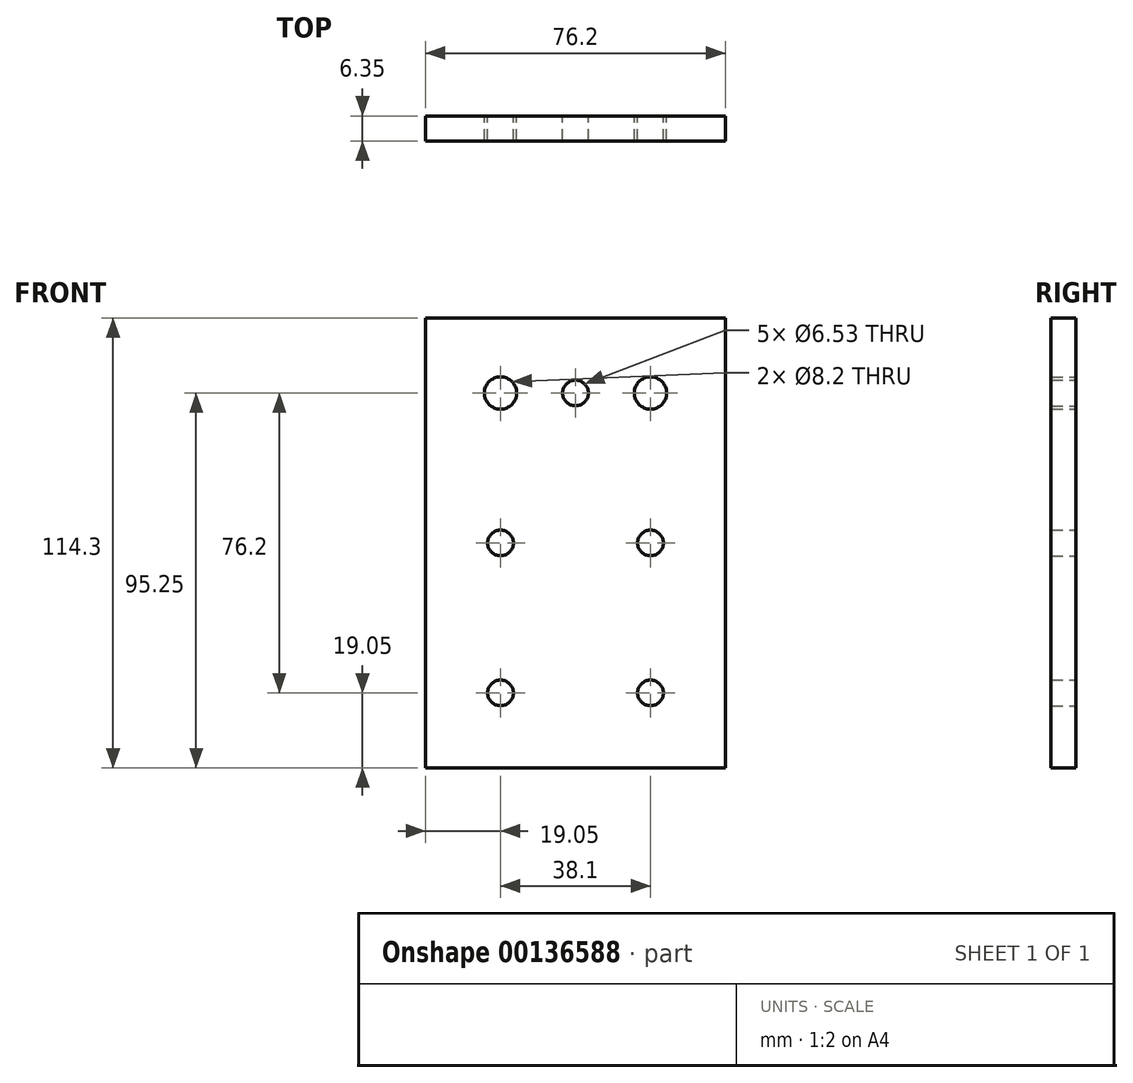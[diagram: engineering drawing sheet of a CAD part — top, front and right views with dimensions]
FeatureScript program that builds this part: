
annotation { "Feature Type Name" : "Feature", "Feature Type Description" : "" }
export const myFeature = defineFeature(function(context is Context, id is Id, definition is map)
    precondition{}
    {
        {
            var Q0;
            Q0=qCreatedBy(makeId("Front.planeOp"),FACE);
            var sketch = newSketch(context, id + "F0", { "sketchPlane" : qUnion([Q0])});
            skLineSegment(sketch, "E0.bottom", {"start": v(0, 0) * mm, "end": v(76.2, 0) * mm});
            skLineSegment(sketch, "E0.top", {"start": v(0, 114.3) * mm, "end": v(76.2, 114.3) * mm});
            skLineSegment(sketch, "E0.left", {"start": v(0, 0) * mm, "end": v(0, 114.3) * mm});
            skLineSegment(sketch, "E0.right", {"start": v(76.2, 0) * mm, "end": v(76.2, 114.3) * mm});
            skCircle(sketch, "E1", {"center": v(19.05, 95.25) * mm, "radius": 4.1 * mm});
            skLineSegment(sketch, "E2", {"start": v(38.1, 114.3) * mm, "end": v(38.1, 0) * mm, "construction": true});
            skCircle(sketch, "E3", {"center": v(19.05, 57.15) * mm, "radius": 3.26 * mm});
            skCircle(sketch, "E4", {"center": v(19.05, 19.05) * mm, "radius": 3.26 * mm});
            skCircle(sketch, "E5.MirrorC", {"center": v(57.15, 95.25) * mm, "radius": 4.1 * mm});
            skCircle(sketch, "E6.MirrorC", {"center": v(57.15, 57.15) * mm, "radius": 3.26 * mm});
            skCircle(sketch, "E7.MirrorC", {"center": v(57.15, 19.05) * mm, "radius": 3.26 * mm});
            skCircle(sketch, "E8", {"center": v(38.1, 95.25) * mm, "radius": 3.26 * mm});
            skSolve(sketch);
        }
        {
            var Q0;
            Q0=makeQuery(id+"F0.imprint","IMPRINT",FACE,{"disambiguationData":[TD([[makeQuery(id+"F0.imprint","IMPRINT",EDGE,{"derivedFrom":sQuery(id+"F0.wireOp",EDGE,"E0.bottom")}),1.0]])]});
            extrude(context, id + "F1", {"entities" : qUnion([Q0]), "depth" : 6.35 * mm});
        }
    });
